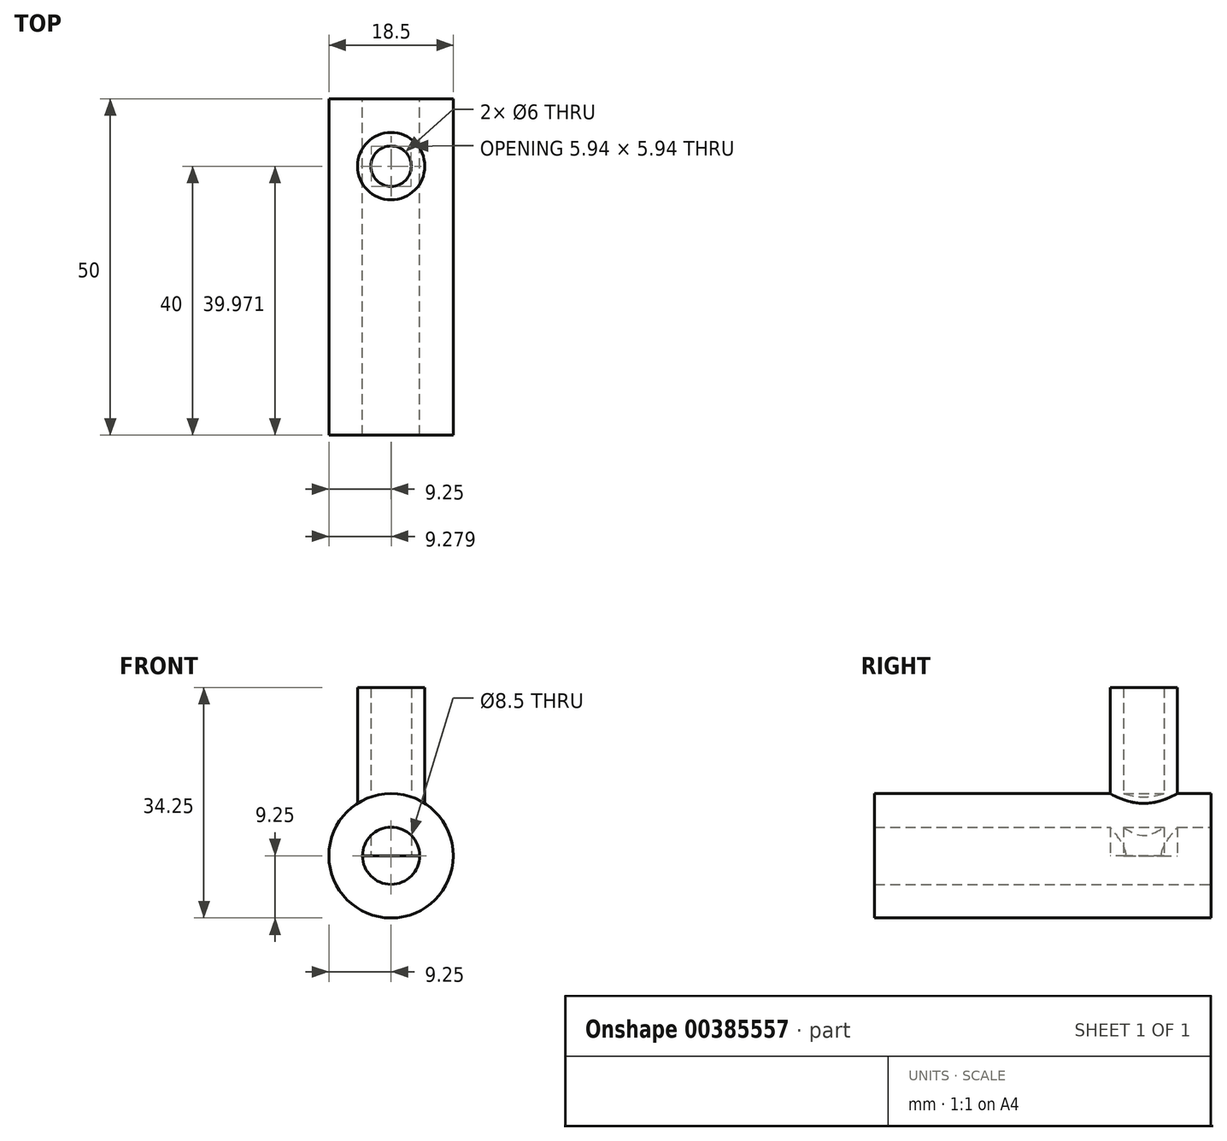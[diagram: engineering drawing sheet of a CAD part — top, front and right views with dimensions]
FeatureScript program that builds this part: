
annotation { "Feature Type Name" : "Feature", "Feature Type Description" : "" }
export const myFeature = defineFeature(function(context is Context, id is Id, definition is map)
    precondition{}
    {
        {
            var Q0;
            Q0=qCreatedBy(makeId("Front.planeOp"),FACE);
            var sketch = newSketch(context, id + "F0", { "sketchPlane" : qUnion([Q0])});
            skCircle(sketch, "E0", {"center": v(0, 0) * mm, "radius": 4.25 * mm});
            skCircle(sketch, "E1", {"center": v(0, 0) * mm, "radius": 9.25 * mm});
            skSolve(sketch);
        }
        {
            var Q0;
            Q0 = qSketchRegion(id + "F0", true);
            extrude(context, id + "F1", {"entities" : qUnion([Q0]), "endBound" : BoundingType.SYMMETRIC, "depth" : 50 * mm});
        }
        {
            var Q0;
            Q0=qCreatedBy(makeId("Top.planeOp"),FACE);
            var sketch = newSketch(context, id + "F2", { "sketchPlane" : qUnion([Q0])});
            skCircle(sketch, "E2", {"center": v(0, 15) * mm, "radius": 3 * mm});
            skCircle(sketch, "E3", {"center": v(0, 15) * mm, "radius": 5 * mm});
            skSolve(sketch);
        }
        {
            var Q0;
            Q0 = qSketchRegion(id + "F2", true);
            extrude(context, id + "F3", {"entities" : qUnion([Q0]), "operationType" : NewBodyOperationType.ADD, "depth" : 25 * mm});
        }
    });
